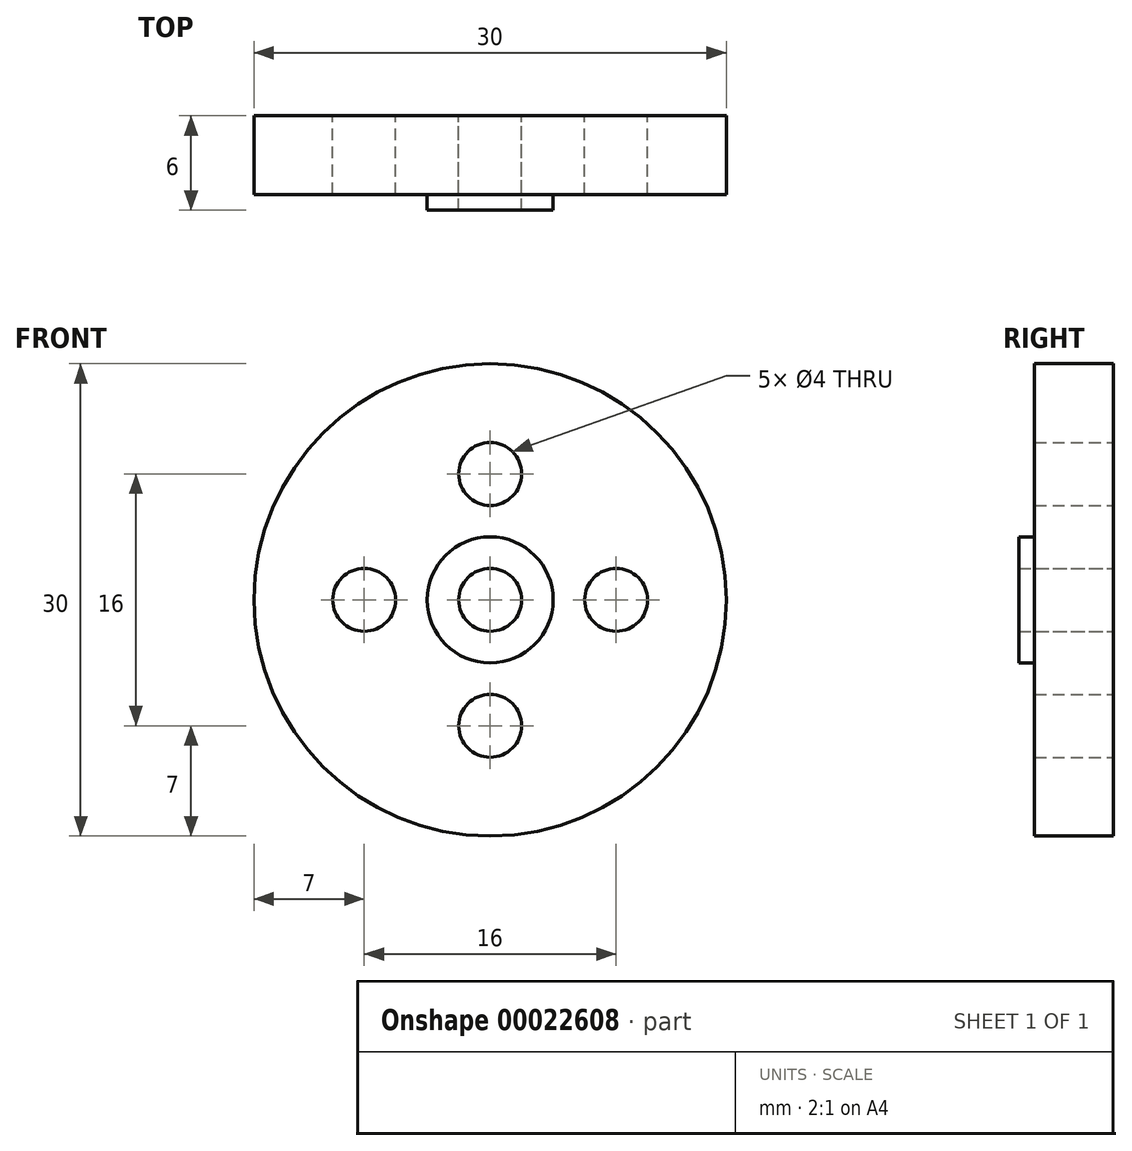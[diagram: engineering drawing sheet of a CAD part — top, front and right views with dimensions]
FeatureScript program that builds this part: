
annotation { "Feature Type Name" : "Feature", "Feature Type Description" : "" }
export const myFeature = defineFeature(function(context is Context, id is Id, definition is map)
    precondition{}
    {
        {
            var Q0;
            Q0=qCreatedBy(makeId("Front.planeOp"),FACE);
            var sketch = newSketch(context, id + "F0", { "sketchPlane" : qUnion([Q0])});
            skCircle(sketch, "E0", {"center": v(0, 0) * mm, "radius": 15 * mm});
            skCircle(sketch, "E1", {"center": v(0, 0) * mm, "radius": 2 * mm});
            skCircle(sketch, "E2", {"center": v(0, 0) * mm, "radius": 4 * mm});
            skLineSegment(sketch, "E3", {"start": v(0, 4) * mm, "end": v(0, 8) * mm});
            skLineSegment(sketch, "E4", {"start": v(-4, 0) * mm, "end": v(-8, 0) * mm});
            skLineSegment(sketch, "E5", {"start": v(0, -4) * mm, "end": v(0, -8) * mm});
            skLineSegment(sketch, "E6", {"start": v(4, 0) * mm, "end": v(8, 0) * mm});
            skCircle(sketch, "E7", {"center": v(0, 8) * mm, "radius": 2 * mm});
            skCircle(sketch, "E8", {"center": v(-8, 0) * mm, "radius": 2 * mm});
            skCircle(sketch, "E9", {"center": v(0, -8) * mm, "radius": 2 * mm});
            skCircle(sketch, "E10", {"center": v(8, 0) * mm, "radius": 2 * mm});
            skSolve(sketch);
        }
        {
            var Q0;
            Q0=makeQuery(id+"F0.imprint","IMPRINT",FACE,{"disambiguationData":[TD([[makeQuery(id+"F0.imprint","IMPRINT",EDGE,{"derivedFrom":sQuery(id+"F0.wireOp",EDGE,"E0")}),1.0]])]});
            extrude(context, id + "F1", {"entities" : qUnion([Q0]), "depth" : 5 * mm});
        }
        {
            var Q0;
            Q0=makeQuery(id+"F0.imprint","IMPRINT",FACE,{"disambiguationData":[TD([[makeQuery(id+"F0.imprint","IMPRINT",EDGE,{"derivedFrom":sQuery(id+"F0.wireOp",EDGE,"E1")}),-1.0]])]});
            extrude(context, id + "F2", {"entities" : qUnion([Q0]), "operationType" : NewBodyOperationType.ADD, "depth" : 6 * mm});
        }
    });
